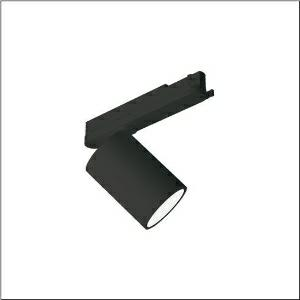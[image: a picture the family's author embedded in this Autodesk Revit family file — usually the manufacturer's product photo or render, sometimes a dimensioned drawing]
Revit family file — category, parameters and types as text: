
# Revit family: spot_31_51sf33mab4b
name_source: partatom
category: Lighting Fixtures
units: mm (PartAtom-declared; Revit-internal decimal feet)

## family parameters
Cut with Voids When Loaded = No
Host = Face
Light Source = No
Part Type = Normal
Room Calculation Point = No
Round Connector Dimension = Use Diameter
Shared = No

## types (1)
- --- (1 x LED, 5030 lm, 41.7 W, 3000K)
    Apparent Load = 42 VA
    CIE Flux Codes = 92 97 99 100 100
    Color Rendering = 90
    Color Temperature = 3000K
    Default Elevation = 1800 mm
    Description = Spot 31, directional spotlight, light control with lens, of PMMA, LED rated luminous flux: 4.830lm, light colour: 930, control gear: ECG Multilumen, with 3-phase adapter, mains connection: 220..240V, AC, 50/60Hz, of aluminium, jet black (RAL 9005), length: 213mm, diameter: 90mm, protection rating (complete): IP20, insulation class (complete): insulation class I (protective earthing), certification: CE, impact resistance: IK02, permissible ambient temperature for indoor applications: -20..+40°C, packaging unit: 1 piece
    Height = 175 mm
    Lamp = 1 x LED
    Lamp Light Flux = 5030 lm
    Lamp Power = 41.7 W
    Lamp count = 1
    Length = 90 mm
    Luminous efficacy = 121 lm/W
    Manufacturer = Siteco
    ModVariant = No
    Model = 51SF33MAB4B
    Mounting Place = Ceiling
    Mounting Type = Pendant
    Number of Poles = 1
    OnlyDefault = Yes
    Power Factor = 1
    Product Name = Spot 31
    Product group = directional spotlight
    ProductGroupID = 905
    Protection Class = Protection class I
    Protection Degree = IP 20
    RLX_Detail_Level = 1
    RLX_Emergency_Light_Flux = 0 lm
    RLX_Emergency_Type = 0
    RLX_Emergency_Type_DB = No
    RlxData = <blob elided: 20881 chars, md5=7879700d>
    Socket = socket
    Standby Power = 0 W
    System Light Flux = 5030 lm
    System Power = 42 W
    Type Comments = factory setting: luminous flux: 100 % | (ON | ON | ON | ON) | 1050 mA
    Type Image = l_1273723.jpg
    URL = http://relux.com
    VarID = @adj_167881
    Voltage = 0 V
    Weight = 0.00 kg
    Width = 0 mm  [stored 0 ft]

note: [stored X ft] marks values corroborated as IEEE doubles in the binary element streams (Revit-internal decimal feet)

## geometry (parser evidence)
native form markers: Blend x4, Sweep x14
no freeform markers — native parametric forms only
